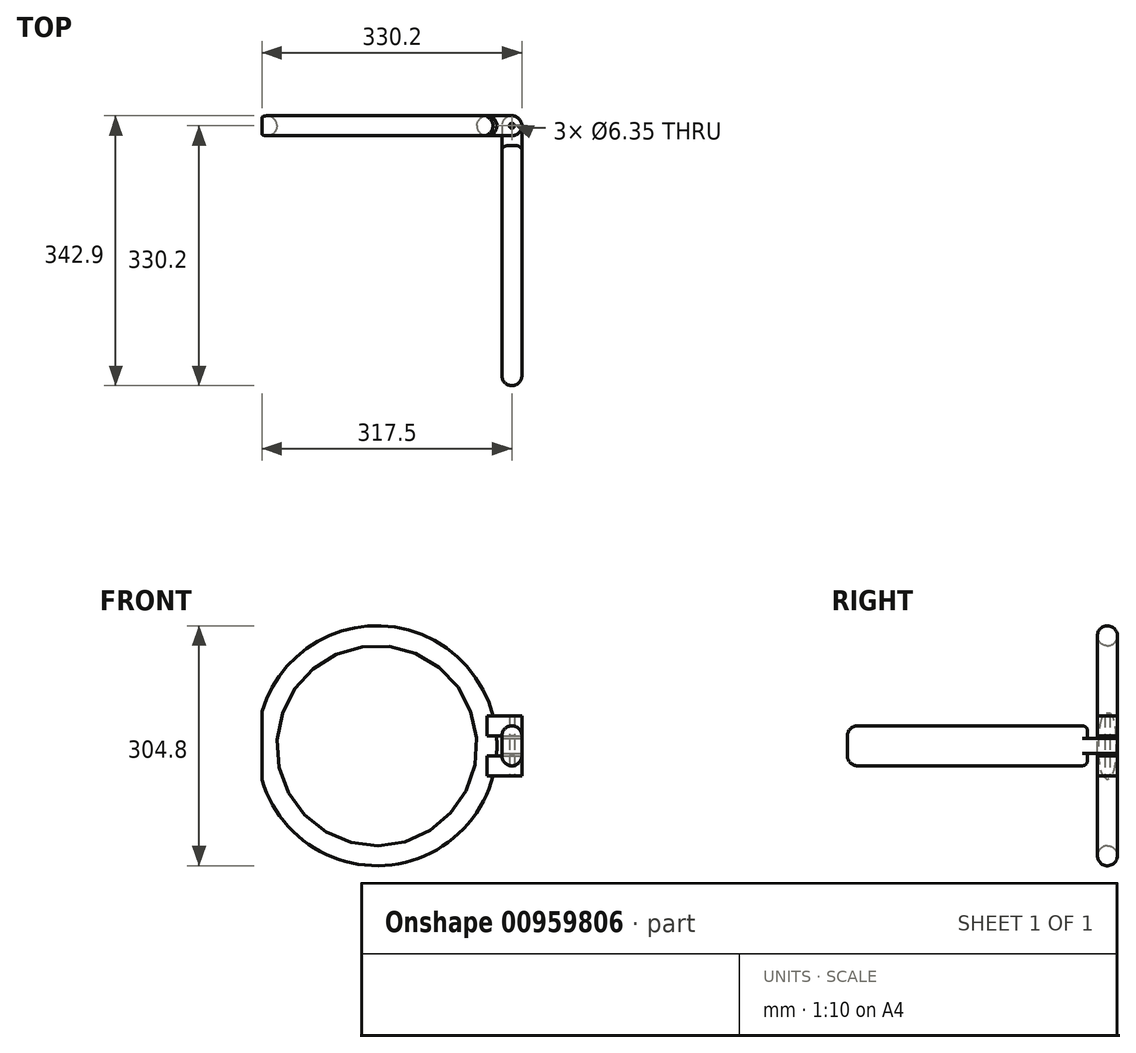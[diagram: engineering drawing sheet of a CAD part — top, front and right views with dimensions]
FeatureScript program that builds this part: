
annotation { "Feature Type Name" : "Feature", "Feature Type Description" : "" }
export const myFeature = defineFeature(function(context is Context, id is Id, definition is map)
    precondition{}
    {
        {
            var Q0;
            Q0=qCreatedBy(makeId("Top.planeOp"),FACE);
            var sketch = newSketch(context, id + "F0", { "sketchPlane" : qUnion([Q0])});
            skCircle(sketch, "E0", {"center": v(139.7, 0) * mm, "radius": 12.7 * mm});
            skLineSegment(sketch, "E1", {"start": v(0, 26.25) * mm, "end": v(0, -24.9) * mm, "construction": true});
            skSolve(sketch);
        }
        {
            var Q0;
            Q0=makeQuery(id+"F0.imprint","IMPRINT",FACE,{"disambiguationData":[TD([[makeQuery(id+"F0.imprint","IMPRINT",EDGE,{"derivedFrom":sQuery(id+"F0.wireOp",EDGE,"E0")}),1.0]])]});
            var Q1;
            Q1=sQuery(id+"F0.wireOp",EDGE,"E1");
            revolve(context, id + "F1", {"surfaceOperationType" : NewSurfaceOperationType.NEW, "entities" : qUnion([Q0]), "axis" : qUnion([Q1]), "revolveType" : RevolveType.FULL});
        }
        {
            var Q0;
            Q0=qCreatedBy(makeId("Front.planeOp"),FACE);
            var sketch = newSketch(context, id + "F2", { "sketchPlane" : qUnion([Q0])});
            skLineSegment(sketch, "E2.bottom", {"start": v(0, -50.8) * mm, "end": v(-146.05, -50.8) * mm});
            skLineSegment(sketch, "E2.top", {"start": v(0, 50.8) * mm, "end": v(-146.05, 50.8) * mm});
            skLineSegment(sketch, "E2.left", {"start": v(0, -50.8) * mm, "end": v(0, 50.8) * mm});
            skLineSegment(sketch, "E2.right", {"start": v(-146.05, -50.8) * mm, "end": v(-146.05, 50.8) * mm});
            skLineSegment(sketch, "E3.bottom", {"start": v(-146.05, 50.8) * mm, "end": v(-155.38, 50.8) * mm});
            skLineSegment(sketch, "E3.top", {"start": v(-146.05, -50.86) * mm, "end": v(-155.38, -50.86) * mm});
            skLineSegment(sketch, "E3.left", {"start": v(-146.05, 50.8) * mm, "end": v(-146.05, -50.86) * mm});
            skLineSegment(sketch, "E3.right", {"start": v(-155.38, 50.8) * mm, "end": v(-155.38, -50.86) * mm});
            skSolve(sketch);
        }
        {
            var Q0;
            {var subQ3=sQuery(id+"F2.wireOp",EDGE,"E3.bottom");Q0=makeQuery(id+"F2.imprint","IMPRINT",FACE,{"disambiguationData":[TD([[makeQuery(id+"F2.imprint","IMPRINT",EDGE,{"derivedFrom":subQ3}),1.0]])]});}
            extrude(context, id + "F3", {"entities" : qUnion([Q0]), "operationType" : NewBodyOperationType.REMOVE, "endBound" : BoundingType.SYMMETRIC, "oppositeDirection" : true, "depth" : 25.4 * mm, "offsetDistance" : 25.4 * mm});
        }
        {
            var Q0;
            Q0=qCreatedBy(makeId("Front.planeOp"),FACE);
            var sketch = newSketch(context, id + "F4", { "sketchPlane" : qUnion([Q0])});
            skLineSegment(sketch, "E4.bottom", {"start": v(139.7, 38.1) * mm, "end": v(184.15, 38.1) * mm});
            skLineSegment(sketch, "E4.top", {"start": v(139.7, 12.7) * mm, "end": v(184.15, 12.7) * mm});
            skLineSegment(sketch, "E4.left", {"start": v(139.7, 38.1) * mm, "end": v(139.7, 12.7) * mm});
            skLineSegment(sketch, "E4.right", {"start": v(184.15, 38.1) * mm, "end": v(184.15, 12.7) * mm});
            skLineSegment(sketch, "E5.bottom", {"start": v(139.7, -38.1) * mm, "end": v(184.15, -38.1) * mm});
            skLineSegment(sketch, "E5.top", {"start": v(139.7, -12.7) * mm, "end": v(184.15, -12.7) * mm});
            skLineSegment(sketch, "E5.left", {"start": v(139.7, -38.1) * mm, "end": v(139.7, -12.7) * mm});
            skLineSegment(sketch, "E5.right", {"start": v(184.15, -38.1) * mm, "end": v(184.15, -12.7) * mm});
            skSolve(sketch);
        }
        {
            var Q0;
            Q0=makeQuery(id+"F4.imprint","IMPRINT",FACE,{"disambiguationData":[TD([[makeQuery(id+"F4.imprint","IMPRINT",EDGE,{"derivedFrom":sQuery(id+"F4.wireOp",EDGE,"E4.bottom")}),-1.0]])]});
            var Q1;
            Q1=makeQuery(id+"F4.imprint","IMPRINT",FACE,{"disambiguationData":[TD([[makeQuery(id+"F4.imprint","IMPRINT",EDGE,{"derivedFrom":sQuery(id+"F4.wireOp",EDGE,"E5.bottom")}),1.0]])]});
            extrude(context, id + "F5", {"entities" : qUnion([Q0, Q1]), "operationType" : NewBodyOperationType.ADD, "depth" : 12.7 * mm, "offsetDistance" : 25.4 * mm, "hasSecondDirection" : true, "secondDirectionOppositeDirection" : true, "secondDirectionDepth" : 12.7 * mm});
        }
        {
            var Q0;
            Q0=makeQuery(id+"F5.opExtrude","SWEPT_FACE",FACE,{"disambiguationData":[OSD([sQuery(id+"F4.wireOp",EDGE,"E4.top")])]});
            var sketch = newSketch(context, id + "F6", { "sketchPlane" : qUnion([Q0])});
            skLineSegment(sketch, "E6.bottom", {"start": v(184.15, 12.7) * mm, "end": v(158.75, 12.7) * mm});
            skLineSegment(sketch, "E6.top", {"start": v(184.15, -12.7) * mm, "end": v(158.75, -12.7) * mm});
            skLineSegment(sketch, "E6.left", {"start": v(184.15, 12.7) * mm, "end": v(184.15, -12.7) * mm});
            skLineSegment(sketch, "E6.right", {"start": v(158.75, 12.7) * mm, "end": v(158.75, -12.7) * mm});
            skSolve(sketch);
        }
        {
            var Q0;
            Q0=makeQuery(id+"F6.imprint","IMPRINT",FACE,{"disambiguationData":[TD([[makeQuery(id+"F6.imprint","IMPRINT",EDGE,{"derivedFrom":sQuery(id+"F6.wireOp",EDGE,"E6.bottom")}),-1.0]])]});
            extrude(context, id + "F7", {"entities" : qUnion([Q0]), "operationType" : NewBodyOperationType.ADD, "depth" : 25.4 * mm, "hasOffset" : true, "offsetDistance" : 3.17 * mm});
        }
        {
            var Q0;
            Q0=makeQuery(id+"F7.boolean.opBoolean","MERGE",FACE,{"derivedFrom":[makeQuery(id+"F5.opExtrude","CAP_FACE",FACE,{"disambiguationData":[OSD([sQuery(id+"F4.wireOp",EDGE,"E4.bottom"),sQuery(id+"F4.wireOp",EDGE,"E4.top"),sQuery(id+"F4.wireOp",EDGE,"E4.left"),sQuery(id+"F4.wireOp",EDGE,"E4.right")])],"isStart":false}),makeQuery(id+"F5.opExtrude","CAP_FACE",FACE,{"disambiguationData":[OSD([sQuery(id+"F4.wireOp",EDGE,"E5.bottom"),sQuery(id+"F4.wireOp",EDGE,"E5.top"),sQuery(id+"F4.wireOp",EDGE,"E5.left"),sQuery(id+"F4.wireOp",EDGE,"E5.right")])],"isStart":false}),makeQuery(id+"F7.opExtrude","SWEPT_FACE",FACE,{"disambiguationData":[OSD([sQuery(id+"F6.wireOp",EDGE,"E6.bottom")])]})]});
            var sketch = newSketch(context, id + "F8", { "sketchPlane" : qUnion([Q0])});
            skLineSegment(sketch, "E7.bottom", {"start": v(158.75, 12.7) * mm, "end": v(184.15, 12.7) * mm});
            skLineSegment(sketch, "E7.top", {"start": v(158.75, 9.53) * mm, "end": v(184.15, 9.53) * mm});
            skLineSegment(sketch, "E7.left", {"start": v(158.75, 12.7) * mm, "end": v(158.75, 9.53) * mm});
            skLineSegment(sketch, "E7.right", {"start": v(184.15, 12.7) * mm, "end": v(184.15, 9.53) * mm});
            skLineSegment(sketch, "E8.bottom", {"start": v(158.75, -12.7) * mm, "end": v(184.15, -12.7) * mm});
            skLineSegment(sketch, "E8.top", {"start": v(158.75, -9.52) * mm, "end": v(184.15, -9.52) * mm});
            skLineSegment(sketch, "E8.left", {"start": v(158.75, -12.7) * mm, "end": v(158.75, -9.52) * mm});
            skLineSegment(sketch, "E8.right", {"start": v(184.15, -12.7) * mm, "end": v(184.15, -9.52) * mm});
            skSolve(sketch);
        }
        {
            var Q0;
            Q0=makeQuery(id+"F8.imprint","IMPRINT",FACE,{"disambiguationData":[TD([[makeQuery(id+"F8.imprint","IMPRINT",EDGE,{"derivedFrom":sQuery(id+"F8.wireOp",EDGE,"E7.bottom")}),-1.0]])]});
            var Q1;
            Q1=makeQuery(id+"F8.imprint","IMPRINT",FACE,{"disambiguationData":[TD([[makeQuery(id+"F8.imprint","IMPRINT",EDGE,{"derivedFrom":sQuery(id+"F8.wireOp",EDGE,"E8.bottom")}),1.0]])]});
            extrude(context, id + "F9", {"entities" : qUnion([Q0, Q1]), "operationType" : NewBodyOperationType.REMOVE, "oppositeDirection" : true, "depth" : 25.4 * mm, "offsetDistance" : 25.4 * mm});
        }
        {
            var Q0;
            Q0=makeQuery(id+"F5.opExtrude","SWEPT_FACE",FACE,{"disambiguationData":[OSD([sQuery(id+"F4.wireOp",EDGE,"E5.bottom")])]});
            var sketch = newSketch(context, id + "F10", { "sketchPlane" : qUnion([Q0])});
            skLineSegment(sketch, "E9", {"start": v(184.15, 0) * mm, "end": v(171.45, 0) * mm});
            skCircle(sketch, "E10", {"center": v(171.45, 0) * mm, "radius": 3.18 * mm});
            skSolve(sketch);
        }
        {
            var Q0;
            Q0=makeQuery(id+"F10.imprint","IMPRINT",FACE,{"disambiguationData":[TD([[makeQuery(id+"F10.imprint","IMPRINT",EDGE,{"derivedFrom":sQuery(id+"F10.wireOp",EDGE,"E10")}),1.0]])]});
            extrude(context, id + "F11", {"entities" : qUnion([Q0]), "operationType" : NewBodyOperationType.REMOVE, "oppositeDirection" : true, "depth" : 80.52 * mm, "offsetDistance" : 25.4 * mm});
        }
        {
            var Q0;
            Q0=makeQuery(id+"F7.opExtrude","SWEPT_EDGE",EDGE,{"disambiguationData":[OSD([sQuery(id+"F4.wireOp",EDGE,"E4.top"),sQuery(id+"F6.wireOp",EDGE,"E6.top"),sQuery(id+"F6.wireOp",EDGE,"E6.right")])]});
            var Q1;
            {var subQ0=sQuery(id+"F4.wireOp",EDGE,"E5.right");var subQ1=sQuery(id+"F4.wireOp",EDGE,"E4.right");var subQ2=sQuery(id+"F6.wireOp",EDGE,"E6.top");var subQ3=sQuery(id+"F6.wireOp",EDGE,"E6.left");Q1=makeQuery(id+"F9.boolean.opBoolean","SPLIT",EDGE,{"disambiguationData":[TD([makeQuery(id+"F9.opExtrude","SWEPT_FACE",FACE,{"disambiguationData":[OSD([sQuery(id+"F8.wireOp",EDGE,"E7.top")])]})])],"derivedFrom":makeQuery(id+"F7.boolean.opBoolean","MERGE",EDGE,{"derivedFrom":[makeQuery(id+"F5.opExtrude","CAP_EDGE",EDGE,{"disambiguationData":[OSD([subQ1])],"isStart":true}),makeQuery(id+"F5.opExtrude","CAP_EDGE",EDGE,{"disambiguationData":[OSD([subQ0])],"isStart":true}),makeQuery(id+"F7.opExtrude","SWEPT_EDGE",EDGE,{"disambiguationData":[OSD([subQ2,subQ3])]})]})});}
            fillet(context, id + "F12", {"entities" : qUnion([Q0, Q1]), "radius" : 12.7 * mm, "tangentPropagation" : true, "allowEdgeOverflow" : false});
        }
        {
            var Q0;
            {var subQ0=sQuery(id+"F4.wireOp",EDGE,"E5.right");var subQ1=sQuery(id+"F4.wireOp",EDGE,"E4.right");Q0=makeQuery(id+"F9.boolean.opBoolean","SPLIT",FACE,{"disambiguationData":[TD([makeQuery(id+"F7.opExtrude","SWEPT_FACE",FACE,{"disambiguationData":[OSD([sQuery(id+"F6.wireOp",EDGE,"E6.right")])]})])],"derivedFrom":makeQuery(id+"F7.boolean.opBoolean","MERGE",FACE,{"derivedFrom":[makeQuery(id+"F5.opExtrude","CAP_FACE",FACE,{"disambiguationData":[OSD([sQuery(id+"F4.wireOp",EDGE,"E4.bottom"),sQuery(id+"F4.wireOp",EDGE,"E4.top"),sQuery(id+"F4.wireOp",EDGE,"E4.left"),subQ1])],"isStart":false}),makeQuery(id+"F5.opExtrude","CAP_FACE",FACE,{"disambiguationData":[OSD([sQuery(id+"F4.wireOp",EDGE,"E5.bottom"),sQuery(id+"F4.wireOp",EDGE,"E5.top"),sQuery(id+"F4.wireOp",EDGE,"E5.left"),subQ0])],"isStart":false}),makeQuery(id+"F7.opExtrude","SWEPT_FACE",FACE,{"disambiguationData":[OSD([sQuery(id+"F6.wireOp",EDGE,"E6.bottom")])]})]})});}
            extrude(context, id + "F13", {"entities" : qUnion([Q0]), "operationType" : NewBodyOperationType.ADD, "depth" : 12.7 * mm, "offsetDistance" : 25.4 * mm});
        }
        {
            var Q0;
            {var subQ1=sQuery(id+"F4.wireOp",EDGE,"E4.right");var subQ2=sQuery(id+"F4.wireOp",EDGE,"E4.bottom");var subQ3=sQuery(id+"F6.wireOp",EDGE,"E6.bottom");var subQ4=sQuery(id+"F4.wireOp",EDGE,"E5.right");var subQ5=sQuery(id+"F6.wireOp",EDGE,"E6.left");Q0=makeQuery(id+"F9.boolean.opBoolean","SPLIT",EDGE,{"disambiguationData":[TD([makeQuery(id+"F5.opExtrude","SWEPT_FACE",FACE,{"disambiguationData":[OSD([subQ2])]})])],"derivedFrom":makeQuery(id+"F7.boolean.opBoolean","MERGE",EDGE,{"derivedFrom":[makeQuery(id+"F5.opExtrude","CAP_EDGE",EDGE,{"disambiguationData":[OSD([subQ1])],"isStart":false}),makeQuery(id+"F5.opExtrude","CAP_EDGE",EDGE,{"disambiguationData":[OSD([subQ4])],"isStart":false}),makeQuery(id+"F7.opExtrude","SWEPT_EDGE",EDGE,{"disambiguationData":[OSD([subQ3,subQ5])]})]})});}
            var Q1;
            {var subQ0=sQuery(id+"F4.wireOp",EDGE,"E5.right");var subQ2=sQuery(id+"F4.wireOp",EDGE,"E5.bottom");var subQ3=sQuery(id+"F4.wireOp",EDGE,"E4.right");var subQ4=sQuery(id+"F6.wireOp",EDGE,"E6.bottom");var subQ5=sQuery(id+"F6.wireOp",EDGE,"E6.left");Q1=makeQuery(id+"F9.boolean.opBoolean","SPLIT",EDGE,{"disambiguationData":[TD([makeQuery(id+"F5.opExtrude","SWEPT_FACE",FACE,{"disambiguationData":[OSD([subQ2])]})])],"derivedFrom":makeQuery(id+"F7.boolean.opBoolean","MERGE",EDGE,{"derivedFrom":[makeQuery(id+"F5.opExtrude","CAP_EDGE",EDGE,{"disambiguationData":[OSD([subQ3])],"isStart":false}),makeQuery(id+"F5.opExtrude","CAP_EDGE",EDGE,{"disambiguationData":[OSD([subQ0])],"isStart":false}),makeQuery(id+"F7.opExtrude","SWEPT_EDGE",EDGE,{"disambiguationData":[OSD([subQ4,subQ5])]})]})});}
            var Q2;
            {var subQ0=sQuery(id+"F4.wireOp",EDGE,"E5.right");var subQ2=sQuery(id+"F4.wireOp",EDGE,"E5.bottom");var subQ3=sQuery(id+"F4.wireOp",EDGE,"E4.right");var subQ4=sQuery(id+"F6.wireOp",EDGE,"E6.left");var subQ5=sQuery(id+"F6.wireOp",EDGE,"E6.top");Q2=makeQuery(id+"F9.boolean.opBoolean","SPLIT",EDGE,{"disambiguationData":[TD([makeQuery(id+"F5.opExtrude","SWEPT_FACE",FACE,{"disambiguationData":[OSD([subQ2])]})])],"derivedFrom":makeQuery(id+"F7.boolean.opBoolean","MERGE",EDGE,{"derivedFrom":[makeQuery(id+"F5.opExtrude","CAP_EDGE",EDGE,{"disambiguationData":[OSD([subQ3])],"isStart":true}),makeQuery(id+"F5.opExtrude","CAP_EDGE",EDGE,{"disambiguationData":[OSD([subQ0])],"isStart":true}),makeQuery(id+"F7.opExtrude","SWEPT_EDGE",EDGE,{"disambiguationData":[OSD([subQ5,subQ4])]})]})});}
            var Q3;
            {var subQ1=sQuery(id+"F4.wireOp",EDGE,"E4.right");var subQ2=sQuery(id+"F4.wireOp",EDGE,"E4.bottom");var subQ3=sQuery(id+"F4.wireOp",EDGE,"E5.right");var subQ4=sQuery(id+"F6.wireOp",EDGE,"E6.top");var subQ5=sQuery(id+"F6.wireOp",EDGE,"E6.left");Q3=makeQuery(id+"F9.boolean.opBoolean","SPLIT",EDGE,{"disambiguationData":[TD([makeQuery(id+"F5.opExtrude","SWEPT_FACE",FACE,{"disambiguationData":[OSD([subQ2])]})])],"derivedFrom":makeQuery(id+"F7.boolean.opBoolean","MERGE",EDGE,{"derivedFrom":[makeQuery(id+"F5.opExtrude","CAP_EDGE",EDGE,{"disambiguationData":[OSD([subQ1])],"isStart":true}),makeQuery(id+"F5.opExtrude","CAP_EDGE",EDGE,{"disambiguationData":[OSD([subQ3])],"isStart":true}),makeQuery(id+"F7.opExtrude","SWEPT_EDGE",EDGE,{"disambiguationData":[OSD([subQ4,subQ5])]})]})});}
            fillet(context, id + "F14", {"entities" : qUnion([Q0, Q1, Q2, Q3]), "radius" : 12.7 * mm, "tangentPropagation" : true, "allowEdgeOverflow" : false});
        }
        {
            var Q0;
            Q0=makeQuery(id+"F13.opExtrude","CAP_FACE",FACE,{"disambiguationData":[OSD([sQuery(id+"F4.wireOp",EDGE,"E4.bottom"),sQuery(id+"F4.wireOp",EDGE,"E4.top"),sQuery(id+"F4.wireOp",EDGE,"E4.left"),sQuery(id+"F4.wireOp",EDGE,"E4.right"),sQuery(id+"F4.wireOp",EDGE,"E5.bottom"),sQuery(id+"F4.wireOp",EDGE,"E5.top"),sQuery(id+"F4.wireOp",EDGE,"E5.left"),sQuery(id+"F4.wireOp",EDGE,"E5.right"),sQuery(id+"F6.wireOp",EDGE,"E6.bottom")])],"isStart":false});
            var sketch = newSketch(context, id + "F15", { "sketchPlane" : qUnion([Q0])});
            skLineSegment(sketch, "E11.bottom", {"start": v(158.75, -25.4) * mm, "end": v(184.15, -25.4) * mm});
            skLineSegment(sketch, "E11.top", {"start": v(158.75, 25.4) * mm, "end": v(184.15, 25.4) * mm});
            skLineSegment(sketch, "E11.left", {"start": v(158.75, -25.4) * mm, "end": v(158.75, 25.4) * mm});
            skLineSegment(sketch, "E11.right", {"start": v(184.15, -25.4) * mm, "end": v(184.15, 25.4) * mm});
            skPoint(sketch, "E11.middle", {"position": v(171.45, 0) * mm});
            skPoint(sketch, "E11.middle.positionSnap0", {"position": v(171.45, -9.52) * mm});
            skPoint(sketch, "E11.centerSnap0", {"position": v(171.45, -9.52) * mm});
            skSolve(sketch);
        }
        {
            var Q0;
            {var subQ0=sQuery(id+"F15.wireOp",EDGE,"E11.top");Q0=makeQuery(id+"F15.imprint","IMPRINT",FACE,{"disambiguationData":[TD([[makeQuery(id+"F15.imprint","IMPRINT",EDGE,{"derivedFrom":subQ0}),-1.0]])]});}
            var Q1;
            {var subQ1=makeQuery(id+"F13.opExtrude","CAP_EDGE",EDGE,{"disambiguationData":[OSD([sQuery(id+"F8.wireOp",EDGE,"E7.top")])],"isStart":false});Q1=makeQuery(id+"F15.imprint","IMPRINT",FACE,{"disambiguationData":[TD([[makeQuery(id+"F15.imprint","IMPRINT",EDGE,{"derivedFrom":subQ1}),-1.0]])]});}
            var Q2;
            {var subQ0=sQuery(id+"F15.wireOp",EDGE,"E11.bottom");Q2=makeQuery(id+"F15.imprint","IMPRINT",FACE,{"disambiguationData":[TD([[makeQuery(id+"F15.imprint","IMPRINT",EDGE,{"derivedFrom":subQ0}),1.0]])]});}
            extrude(context, id + "F16", {"entities" : qUnion([Q0, Q1, Q2]), "operationType" : NewBodyOperationType.ADD, "depth" : 304.8 * mm, "offsetDistance" : 25.4 * mm});
        }
        {
            var Q0;
            Q0=makeQuery(id+"F16.opExtrude","SWEPT_EDGE",EDGE,{"disambiguationData":[OSD([sQuery(id+"F15.wireOp",EDGE,"E11.bottom"),sQuery(id+"F15.wireOp",EDGE,"E11.left")])]});
            var Q1;
            Q1=makeQuery(id+"F16.opExtrude","SWEPT_EDGE",EDGE,{"disambiguationData":[OSD([sQuery(id+"F15.wireOp",EDGE,"E11.bottom"),sQuery(id+"F15.wireOp",EDGE,"E11.right")])]});
            var Q2;
            Q2=makeQuery(id+"F16.opExtrude","SWEPT_EDGE",EDGE,{"disambiguationData":[OSD([sQuery(id+"F15.wireOp",EDGE,"E11.top"),sQuery(id+"F15.wireOp",EDGE,"E11.right")])]});
            var Q3;
            Q3=makeQuery(id+"F16.opExtrude","SWEPT_EDGE",EDGE,{"disambiguationData":[OSD([sQuery(id+"F15.wireOp",EDGE,"E11.top"),sQuery(id+"F15.wireOp",EDGE,"E11.left")])]});
            fillet(context, id + "F17", {"entities" : qUnion([Q0, Q1, Q2, Q3]), "radius" : 12.7 * mm, "tangentPropagation" : true, "allowEdgeOverflow" : false});
        }
        {
            var Q0;
            {var subQ0=sQuery(id+"F15.wireOp",EDGE,"E11.bottom");var subQ5=sQuery(id+"F15.wireOp",EDGE,"E11.left");var subQ7=sQuery(id+"F8.wireOp",EDGE,"E8.top");var subQ8=sQuery(id+"F15.wireOp",EDGE,"E11.right");Q0=makeQuery(id+"F17.opFillet","BLEND_EDGE",EDGE,{"blendedFrom":[makeQuery(id+"F16.opExtrude","SWEPT_EDGE",EDGE,{"disambiguationData":[OSD([subQ0,subQ5])]}),makeQuery(id+"F16.boolean.opBoolean","SPLIT",FACE,{"disambiguationData":[TD([makeQuery(id+"F9.boolean.opBoolean","COPY",FACE,{"derivedFrom":makeQuery(id+"F9.opExtrude","SWEPT_FACE",FACE,{"disambiguationData":[OSD([subQ7])]})})])],"derivedFrom":makeQuery(id+"F16.opExtrude","CAP_FACE",FACE,{"disambiguationData":[OSD([subQ0,sQuery(id+"F15.wireOp",EDGE,"E11.top"),subQ5,subQ8])],"isStart":true})})],"blendedInto":[makeQuery(id+"F16.boolean.opBoolean","SPLIT",FACE,{"disambiguationData":[TD([makeQuery(id+"F9.boolean.opBoolean","COPY",FACE,{"derivedFrom":makeQuery(id+"F9.opExtrude","SWEPT_FACE",FACE,{"disambiguationData":[OSD([subQ7])]})})])],"derivedFrom":makeQuery(id+"F16.opExtrude","CAP_FACE",FACE,{"disambiguationData":[OSD([subQ0,sQuery(id+"F15.wireOp",EDGE,"E11.top"),subQ5,subQ8])],"isStart":true})})]});}
            var Q1;
            {var subQ0=sQuery(id+"F15.wireOp",EDGE,"E11.top");var subQ6=sQuery(id+"F15.wireOp",EDGE,"E11.left");var subQ7=sQuery(id+"F8.wireOp",EDGE,"E7.top");var subQ8=sQuery(id+"F15.wireOp",EDGE,"E11.right");Q1=makeQuery(id+"F17.opFillet","BLEND_EDGE",EDGE,{"blendedFrom":[makeQuery(id+"F16.opExtrude","SWEPT_EDGE",EDGE,{"disambiguationData":[OSD([subQ0,subQ6])]}),makeQuery(id+"F16.boolean.opBoolean","SPLIT",FACE,{"disambiguationData":[TD([makeQuery(id+"F9.boolean.opBoolean","COPY",FACE,{"derivedFrom":makeQuery(id+"F9.opExtrude","SWEPT_FACE",FACE,{"disambiguationData":[OSD([subQ7])]})})])],"derivedFrom":makeQuery(id+"F16.opExtrude","CAP_FACE",FACE,{"disambiguationData":[OSD([sQuery(id+"F15.wireOp",EDGE,"E11.bottom"),subQ0,subQ6,subQ8])],"isStart":true})})],"blendedInto":[makeQuery(id+"F16.boolean.opBoolean","SPLIT",FACE,{"disambiguationData":[TD([makeQuery(id+"F9.boolean.opBoolean","COPY",FACE,{"derivedFrom":makeQuery(id+"F9.opExtrude","SWEPT_FACE",FACE,{"disambiguationData":[OSD([subQ7])]})})])],"derivedFrom":makeQuery(id+"F16.opExtrude","CAP_FACE",FACE,{"disambiguationData":[OSD([sQuery(id+"F15.wireOp",EDGE,"E11.bottom"),subQ0,subQ6,subQ8])],"isStart":true})})]});}
            fillet(context, id + "F18", {"entities" : qUnion([Q0, Q1]), "radius" : 6.35 * mm, "tangentPropagation" : true, "allowEdgeOverflow" : false});
        }
        {
            var Q0;
            Q0=makeQuery(id+"F16.opExtrude","CAP_EDGE",EDGE,{"disambiguationData":[OSD([sQuery(id+"F15.wireOp",EDGE,"E11.left")])],"isStart":false});
            fillet(context, id + "F19", {"entities" : qUnion([Q0]), "radius" : 12.7 * mm, "tangentPropagation" : true, "allowEdgeOverflow" : false});
        }
    });
